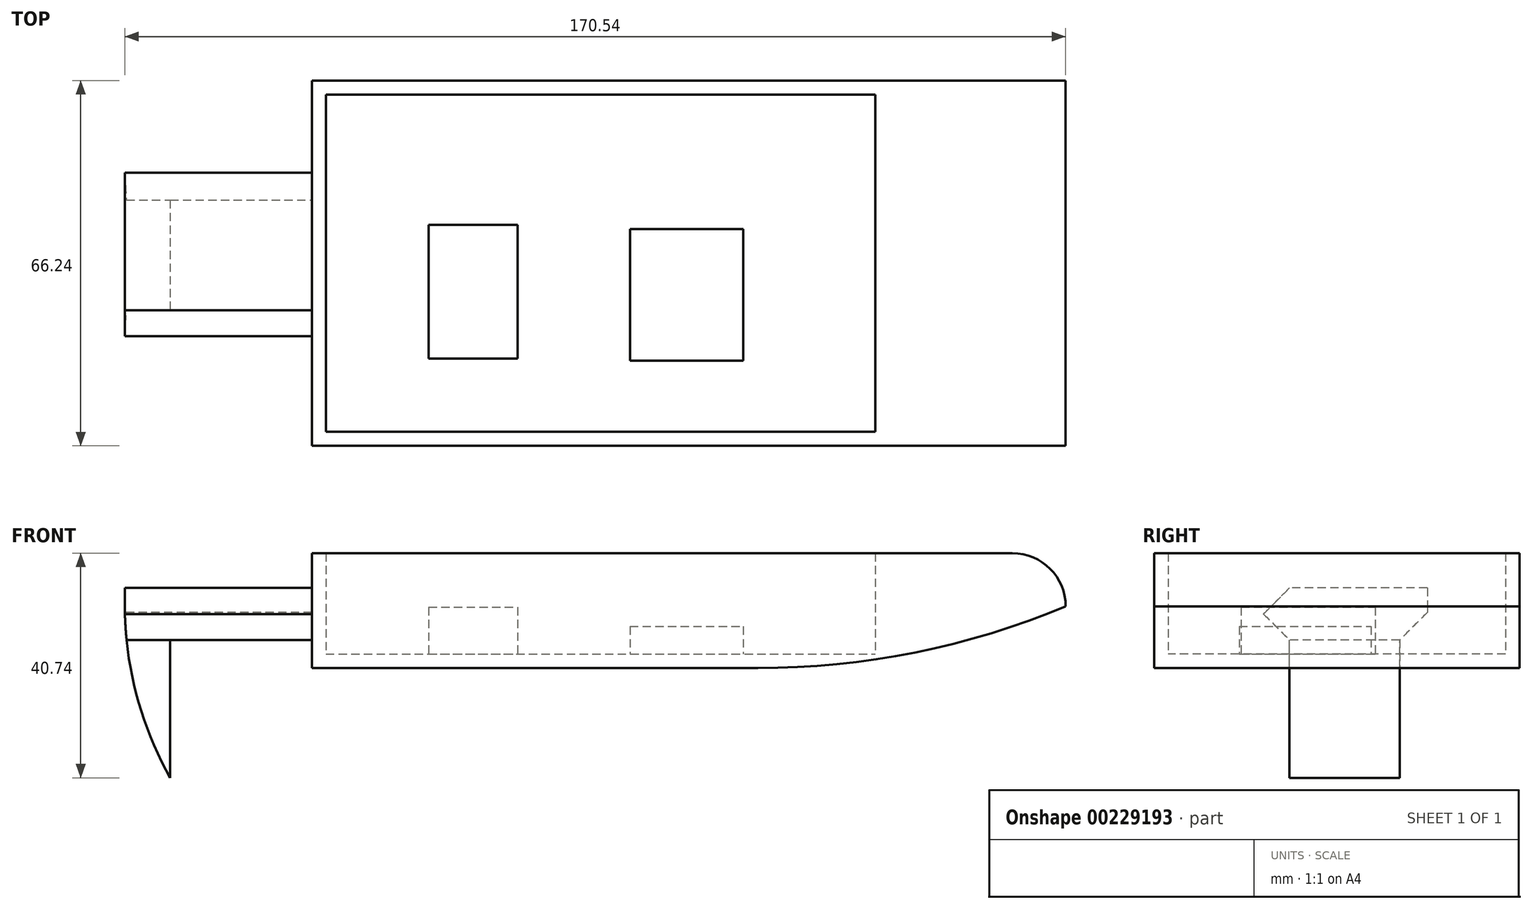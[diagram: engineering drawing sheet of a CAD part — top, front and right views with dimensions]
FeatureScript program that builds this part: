
annotation { "Feature Type Name" : "Feature", "Feature Type Description" : "" }
export const myFeature = defineFeature(function(context is Context, id is Id, definition is map)
    precondition{}
    {
        {
            var Q0;
            Q0=qCreatedBy(makeId("Top.planeOp"),FACE);
            var sketch = newSketch(context, id + "F0", { "sketchPlane" : qUnion([Q0])});
            skLineSegment(sketch, "E0.bottom", {"start": v(0, 0) * mm, "end": v(104.64, 0) * mm});
            skLineSegment(sketch, "E0.top", {"start": v(0, -66.24) * mm, "end": v(104.64, -66.24) * mm});
            skLineSegment(sketch, "E0.left", {"start": v(0, 0) * mm, "end": v(0, -66.24) * mm});
            skLineSegment(sketch, "E0.right", {"start": v(104.64, 0) * mm, "end": v(104.64, -66.24) * mm});
            skSolve(sketch);
        }
        {
            var Q0;
            Q0=makeQuery(id+"F0.imprint","IMPRINT",FACE,{"disambiguationData":[TD([[makeQuery(id+"F0.imprint","IMPRINT",EDGE,{"derivedFrom":sQuery(id+"F0.wireOp",EDGE,"E0.bottom")}),-1.0]])]});
            extrude(context, id + "F1", {"entities" : qUnion([Q0]), "depth" : 20.83 * mm});
        }
        {
            var Q0;
            Q0=makeQuery(id+"F1.opExtrude","CAP_FACE",FACE,{"disambiguationData":[OSD([sQuery(id+"F0.wireOp",EDGE,"E0.bottom"),sQuery(id+"F0.wireOp",EDGE,"E0.top"),sQuery(id+"F0.wireOp",EDGE,"E0.left"),sQuery(id+"F0.wireOp",EDGE,"E0.right")])],"isStart":false});
            shell(context, id + "F2", {"entities" : qUnion([Q0]), "thickness" : 2.54 * mm});
        }
        {
            var Q0;
            Q0=makeQuery(id+"F1.opExtrude","SWEPT_FACE",FACE,{"disambiguationData":[OSD([sQuery(id+"F0.wireOp",EDGE,"E0.right")])]});
            var sketch = newSketch(context, id + "F3", { "sketchPlane" : qUnion([Q0])});
            skLineSegment(sketch, "E1.bottom", {"start": v(-66.24, 20.83) * mm, "end": v(0, 20.83) * mm});
            skLineSegment(sketch, "E1.top", {"start": v(-66.24, 0) * mm, "end": v(0, 0) * mm});
            skLineSegment(sketch, "E1.left", {"start": v(-66.24, 20.83) * mm, "end": v(-66.24, 0) * mm});
            skLineSegment(sketch, "E1.right", {"start": v(0, 20.83) * mm, "end": v(0, 0) * mm});
            skSolve(sketch);
        }
        {
            var Q0;
            Q0 = qSketchRegion(id + "F3", true);
            extrude(context, id + "F4", {"entities" : qUnion([Q0]), "operationType" : NewBodyOperationType.ADD, "depth" : 32 * mm});
        }
        {
            var Q0;
            Q0=makeQuery(id+"F4.opExtrude","CAP_EDGE",EDGE,{"disambiguationData":[OSD([sQuery(id+"F3.wireOp",EDGE,"E1.bottom")])],"isStart":false});
            fillet(context, id + "F5", {"entities" : qUnion([Q0]), "radius" : 9.66 * mm, "tangentPropagation" : true, "allowEdgeOverflow" : false});
        }
        {
            var Q0;
            Q0=makeQuery(id+"F4.opExtrude","CAP_EDGE",EDGE,{"disambiguationData":[OSD([sQuery(id+"F3.wireOp",EDGE,"E1.top")])],"isStart":false});
            fillet(context, id + "F6", {"entities" : qUnion([Q0]), "radius" : 144.85 * mm, "tangentPropagation" : true, "allowEdgeOverflow" : false});
        }
        {
            var Q0;
            Q0=makeQuery(id+"F2.opShell","OFFSET_FACE",FACE,{"disambiguationData":[OSD([sQuery(id+"F0.wireOp",EDGE,"E0.bottom"),sQuery(id+"F0.wireOp",EDGE,"E0.top"),sQuery(id+"F0.wireOp",EDGE,"E0.left"),sQuery(id+"F0.wireOp",EDGE,"E0.right")])]});
            var sketch = newSketch(context, id + "F7", { "sketchPlane" : qUnion([Q0])});
            skLineSegment(sketch, "E2.bottom", {"start": v(57.65, -50.79) * mm, "end": v(78.2, -50.79) * mm});
            skLineSegment(sketch, "E2.top", {"start": v(57.65, -26.92) * mm, "end": v(78.2, -26.92) * mm});
            skLineSegment(sketch, "E2.left", {"start": v(57.65, -50.79) * mm, "end": v(57.65, -26.92) * mm});
            skLineSegment(sketch, "E2.right", {"start": v(78.2, -50.79) * mm, "end": v(78.2, -26.92) * mm});
            skSolve(sketch);
        }
        {
            var Q0;
            Q0=makeQuery(id+"F7.imprint","IMPRINT",FACE,{"disambiguationData":[TD([[makeQuery(id+"F7.imprint","IMPRINT",EDGE,{"derivedFrom":sQuery(id+"F7.wireOp",EDGE,"E2.bottom")}),1.0]])]});
            extrude(context, id + "F8", {"entities" : qUnion([Q0]), "operationType" : NewBodyOperationType.ADD, "depth" : 5 * mm});
        }
        {
            var Q0;
            Q0=makeQuery(id+"F2.opShell","OFFSET_FACE",FACE,{"disambiguationData":[OSD([sQuery(id+"F0.wireOp",EDGE,"E0.bottom"),sQuery(id+"F0.wireOp",EDGE,"E0.top"),sQuery(id+"F0.wireOp",EDGE,"E0.left"),sQuery(id+"F0.wireOp",EDGE,"E0.right")])]});
            var sketch = newSketch(context, id + "F9", { "sketchPlane" : qUnion([Q0])});
            skLineSegment(sketch, "E3.bottom", {"start": v(21.17, -50.43) * mm, "end": v(37.26, -50.43) * mm});
            skLineSegment(sketch, "E3.top", {"start": v(21.17, -26.16) * mm, "end": v(37.26, -26.16) * mm});
            skLineSegment(sketch, "E3.left", {"start": v(21.17, -50.43) * mm, "end": v(21.17, -26.16) * mm});
            skLineSegment(sketch, "E3.right", {"start": v(37.26, -50.43) * mm, "end": v(37.26, -26.16) * mm});
            skSolve(sketch);
        }
        {
            var Q0;
            Q0=makeQuery(id+"F9.imprint","IMPRINT",FACE,{"disambiguationData":[TD([[makeQuery(id+"F9.imprint","IMPRINT",EDGE,{"derivedFrom":sQuery(id+"F9.wireOp",EDGE,"E3.bottom")}),1.0]])]});
            extrude(context, id + "F10", {"entities" : qUnion([Q0]), "operationType" : NewBodyOperationType.ADD, "depth" : 8.5 * mm});
        }
        {
            var Q0;
            Q0=makeQuery(id+"F1.opExtrude","SWEPT_FACE",FACE,{"disambiguationData":[OSD([sQuery(id+"F0.wireOp",EDGE,"E0.left")])]});
            var sketch = newSketch(context, id + "F11", { "sketchPlane" : qUnion([Q0])});
            skLineSegment(sketch, "E4.bottom", {"start": v(16.7, 14.53) * mm, "end": v(46.68, 14.53) * mm});
            skLineSegment(sketch, "E4.top", {"start": v(16.7, 5.1) * mm, "end": v(46.68, 5.1) * mm});
            skLineSegment(sketch, "E4.left", {"start": v(16.7, 14.53) * mm, "end": v(16.7, 5.1) * mm});
            skLineSegment(sketch, "E4.right", {"start": v(46.68, 14.53) * mm, "end": v(46.68, 5.1) * mm});
            skSolve(sketch);
        }
        {
            var Q0;
            Q0=makeQuery(id+"F11.imprint","IMPRINT",FACE,{"disambiguationData":[TD([[makeQuery(id+"F11.imprint","IMPRINT",EDGE,{"derivedFrom":sQuery(id+"F11.wireOp",EDGE,"E4.bottom")}),-1.0]])]});
            extrude(context, id + "F12", {"entities" : qUnion([Q0]), "operationType" : NewBodyOperationType.ADD, "depth" : 33.9 * mm});
        }
        {
            var Q0;
            Q0=makeQuery(id+"F12.opExtrude","SWEPT_EDGE",EDGE,{"disambiguationData":[OSD([sQuery(id+"F11.wireOp",EDGE,"E4.top"),sQuery(id+"F11.wireOp",EDGE,"E4.right")])]});
            var Q1;
            Q1=makeQuery(id+"F12.opExtrude","SWEPT_EDGE",EDGE,{"disambiguationData":[OSD([sQuery(id+"F11.wireOp",EDGE,"E4.top"),sQuery(id+"F11.wireOp",EDGE,"E4.left")])]});
            var Q2;
            Q2=makeQuery(id+"F12.opExtrude","SWEPT_EDGE",EDGE,{"disambiguationData":[OSD([sQuery(id+"F11.wireOp",EDGE,"E4.bottom"),sQuery(id+"F11.wireOp",EDGE,"E4.right")])]});
            chamfer(context, id + "F13", {"entities" : qUnion([Q0, Q1, Q2]), "width" : 5 * mm, "tangentPropagation" : true});
        }
        {
            var Q0;
            Q0=makeQuery(id+"F12.opExtrude","SWEPT_FACE",FACE,{"disambiguationData":[OSD([sQuery(id+"F11.wireOp",EDGE,"E4.top")])]});
            var sketch = newSketch(context, id + "F14", { "sketchPlane" : qUnion([Q0])});
            skLineSegment(sketch, "E5.bottom", {"start": v(-33.9, 21.7) * mm, "end": v(-25.68, 21.7) * mm});
            skLineSegment(sketch, "E5.top", {"start": v(-33.9, 41.68) * mm, "end": v(-25.68, 41.68) * mm});
            skLineSegment(sketch, "E5.left", {"start": v(-33.9, 21.7) * mm, "end": v(-33.9, 41.68) * mm});
            skLineSegment(sketch, "E5.right", {"start": v(-25.68, 21.7) * mm, "end": v(-25.68, 41.68) * mm});
            skSolve(sketch);
        }
        {
            var Q0;
            Q0=makeQuery(id+"F14.imprint","IMPRINT",FACE,{"disambiguationData":[TD([[makeQuery(id+"F14.imprint","IMPRINT",EDGE,{"derivedFrom":sQuery(id+"F14.wireOp",EDGE,"E5.bottom")}),1.0]])]});
            extrude(context, id + "F15", {"entities" : qUnion([Q0]), "operationType" : NewBodyOperationType.ADD, "depth" : 25 * mm});
        }
        {
            var Q0;
            Q0=makeQuery(id+"F15.opExtrude","CAP_EDGE",EDGE,{"disambiguationData":[OSD([sQuery(id+"F14.wireOp",EDGE,"E5.left")])],"isStart":false});
            fillet(context, id + "F16", {"entities" : qUnion([Q0]), "radius" : 63.98 * mm, "tangentPropagation" : true, "allowEdgeOverflow" : false});
        }
    });
